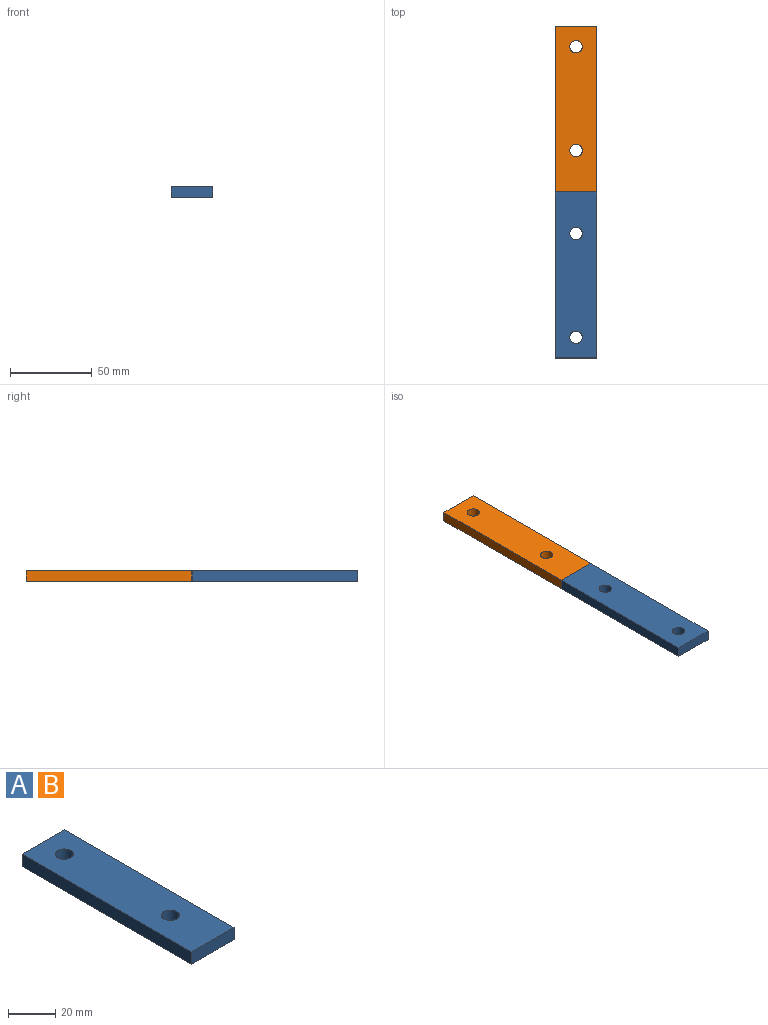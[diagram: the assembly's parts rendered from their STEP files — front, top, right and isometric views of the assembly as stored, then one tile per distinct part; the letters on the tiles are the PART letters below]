
ASSEMBLY  parts=2 mates=1
PART A: 8 faces, bbox 25.4x101.6x6.4 mm
  f0: plane 25.4x6.35mm, normal (0,-1,0), area 161.3mm2, adj f1,f5,f6,f7
  f1: plane 101.6x6.35mm, normal (1,0,0), area 645.2mm2, adj f0,f2,f6,f7
  f2: plane 25.4x6.35mm, normal (0,1,0), area 161.3mm2, adj f1,f5,f6,f7
  f3: cylinder r=3.81mm len=7.62mm, axis (0,0,-1), area 152mm2, adj f6,f7
  f4: cylinder r=3.81mm len=7.62mm, axis (0,0,-1), area 152mm2, adj f6,f7
  f5: plane 101.6x6.35mm, normal (-1,0,0), area 645.2mm2, adj f0,f2,f6,f7
  f6: plane 101.6x25.4mm, normal (0,0,1), area 2489.4mm2, adj f0,f1,f2,f3,f4,f5
  f7: plane 101.6x25.4mm, normal (0,0,-1), area 2489.4mm2, adj f0,f1,f2,f3,f4,f5
PART B: same geometry as A
PLACE A rot(axis=(1,0,0),180deg) t=(43.82,-50.05,4.45)mm
PLACE B t=(43.82,0.75,-1.9)mm
MATE fastened A.f0 <-> B.f0  axis (0,1,0) through (43.82,-24.65,1.27)mm
